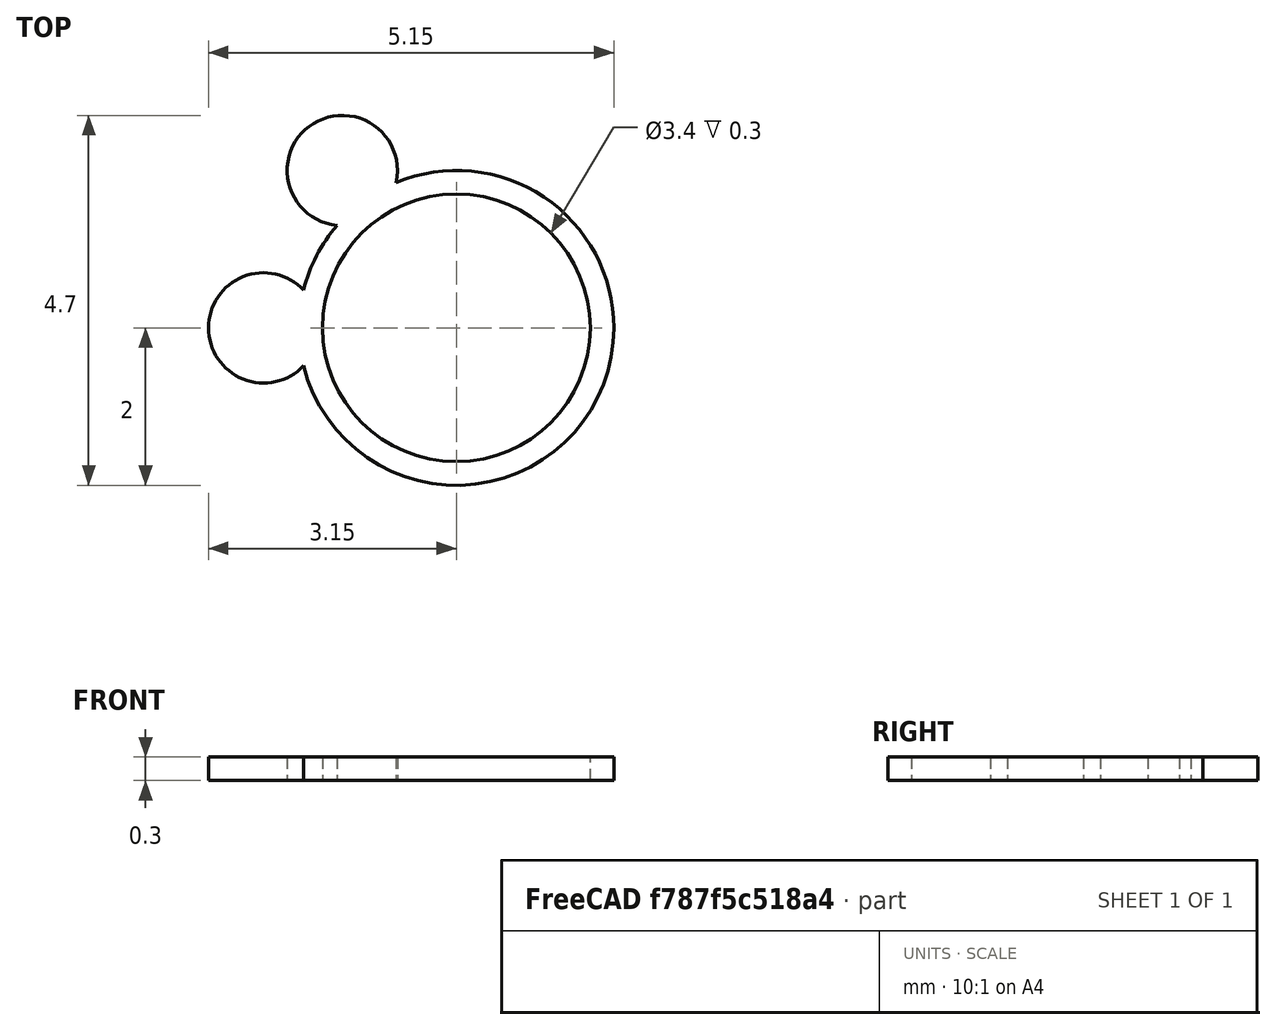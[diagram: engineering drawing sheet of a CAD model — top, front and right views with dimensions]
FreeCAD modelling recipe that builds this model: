
FCSTD DOCUMENT  (FreeCAD 1.0R38806 (Git))
Label: reto_6
License: All rights reserved
LicenseURL: https://en.wikipedia.org/wiki/All_rights_reserved
objects: Part::Cylinder×4, Part::Fuse×2, Part::Cut×1
note: 7 computed .brp shape members not serialized (recipe doc carries the construction recipe); baked Part::Feature solids carry a one-line shape summary decoded from their .brp

FEATURE [Part::Cylinder] Cylinder
  Angle = 360
  AttacherType = Attacher::AttachEngine3D
  FirstAngle = 0
  Height = 0.3
  Radius = 2
  SecondAngle = 0
FEATURE [Part::Cylinder] Cylinder001
  Angle = 360
  AttacherType = Attacher::AttachEngine3D
  FirstAngle = 0
  Height = 1
  Placement = pos=(0,0,-0.5) rot=(0,0,1;0rad)
  Radius = 1.7
  SecondAngle = 0
FEATURE [Part::Cut] Cut
  Base = -> Cylinder
  Refine = true
  Tool = -> Cylinder001
FEATURE [Part::Cylinder] Cylinder002
  Angle = 360
  AttacherType = Attacher::AttachEngine3D
  FirstAngle = 0
  Height = 0.3
  Placement = pos=(-1.45,2,0) rot=(0,0,1;0rad)
  Radius = 0.7
  SecondAngle = 0
FEATURE [Part::Cylinder] Cylinder003
  Angle = 360
  AttacherType = Attacher::AttachEngine3D
  FirstAngle = 0
  Height = 0.3
  Placement = pos=(-2.45,0,0) rot=(0,0,1;0rad)
  Radius = 0.7
  SecondAngle = 0
FEATURE [Part::Fuse] Fusion
  Base = -> Cut
  Refine = true
  Tool = -> Cylinder002
FEATURE [Part::Fuse] Fusion001
  Base = -> Fusion
  Refine = true
  Tool = -> Cylinder003
